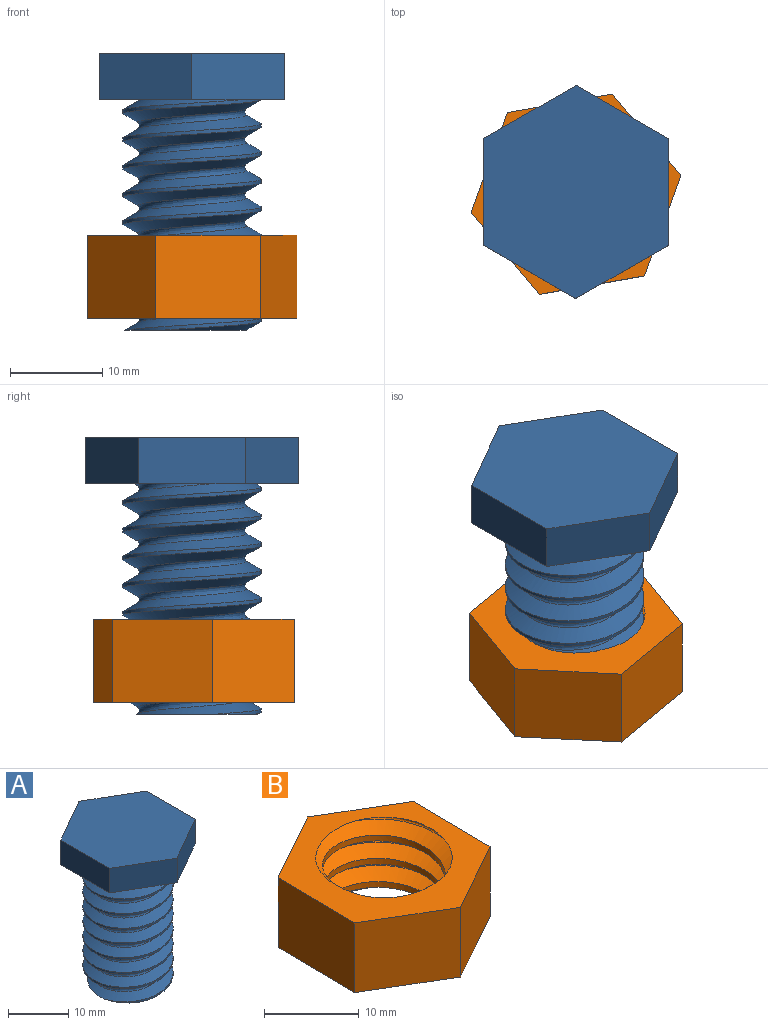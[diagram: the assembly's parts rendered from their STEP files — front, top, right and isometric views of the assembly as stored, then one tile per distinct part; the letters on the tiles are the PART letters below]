
ASSEMBLY  parts=2 mates=1
PART A: 13 faces, bbox 20.8x23.9x32.3 mm
  f0: cylinder r=7.5mm len=25mm, axis (0,0,1), area 114.5mm2, adj f1,f9,f11,f12
  f1: plane 13.99x13.98mm, normal (0,0,-1), area 136.5mm2, adj f0,f10,f11,f12
  f2: plane 11.55x5mm, normal (1,0,0), area 57.7mm2, adj f3,f7,f8,f9
  f3: plane 9.99x5.79mm, normal (0.5,0.87,0), area 57.7mm2, adj f2,f4,f8,f9
  f4: plane 10.01x5.76mm, normal (-0.5,0.87,0), area 57.7mm2, adj f3,f5,f8,f9
  f5: plane 11.55x5mm, normal (-1,0,0), area 57.7mm2, adj f4,f6,f8,f9
  f6: plane 9.99x5.79mm, normal (-0.5,-0.87,0), area 57.7mm2, adj f5,f7,f8,f9
  f7: plane 10.01x5.76mm, normal (0.5,-0.87,0), area 57.7mm2, adj f2,f6,f8,f9
  f8: plane 23.09x20.02mm, normal (0,0,1), area 346.4mm2, adj f2,f3,f4,f5,f6,f7
  f9: plane 23.91x20.83mm, normal (0,0,-1), area 210mm2, adj f0,f2,f3,f4,f5,f6,f7,f10
  f10: bspline ~27.25x13.57mm, area 253.8mm2, adj f1,f9,f11,f12
  f11: bspline ~27.44x17.32mm, area 657.7mm2, adj f0,f1,f9,f10
  f12: bspline ~27.44x17.32mm, area 658.7mm2, adj f0,f1,f9,f10
PART B: 12 faces, bbox 21x23.9x12.3 mm
  f0: plane 11.55x9mm, normal (1,-0.01,0), area 103.9mm2, adj f1,f5,f6,f7
  f1: plane 9.93x9mm, normal (0.51,0.86,0), area 103.9mm2, adj f0,f2,f6,f7
  f2: plane 10.07x9mm, normal (-0.49,0.87,0), area 103.9mm2, adj f1,f3,f6,f7
  f3: plane 11.55x9mm, normal (-1,0.01,0), area 103.9mm2, adj f2,f4,f6,f7
  f4: plane 9.93x9mm, normal (-0.51,-0.86,0), area 103.9mm2, adj f3,f5,f6,f7
  f5: plane 10.07x9mm, normal (0.49,-0.87,0), area 103.9mm2, adj f0,f4,f6,f7
  f6: plane 23.95x20.99mm, normal (0,0,1), area 181.5mm2, adj f0,f1,f2,f3,f4,f5,f8,f9
  f7: plane 23.95x20.99mm, normal (0,0,-1), area 181.5mm2, adj f0,f1,f2,f3,f4,f5,f8,f9
  f8: bspline ~18.76x16.25mm, area 258.9mm2, adj f6,f7,f10,f11
  f9: bspline ~18.76x16.25mm, area 258.9mm2, adj f6,f7,f10,f11
  f10: bspline ~19.08x16.52mm, area 67.1mm2, adj f6,f7,f8,f9
  f11: cylinder r=6.5mm len=13mm, axis (0,0,1), area 92.2mm2, adj f6,f7,f8,f9
PLACE A t=(-7.28,-4.62,9.91)mm fixed
PLACE B rot(axis=(0,0,-1),19.3deg) t=(-7.28,-4.83,-13.75)mm
MATE cylindrical A.f1 <-> B.f7  axis (0,0,-1) through (-8,-5.18,-15.09)mm
